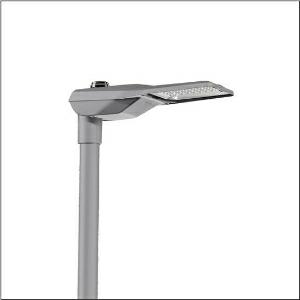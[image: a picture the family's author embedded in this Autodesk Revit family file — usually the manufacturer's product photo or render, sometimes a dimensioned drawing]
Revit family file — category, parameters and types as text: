
# Revit family: streetlight_sl_21_mini___p1_0a_5xe6a37n08hb_d726
name_source: partatom
category: Lighting Fixtures
units: mm (PartAtom-declared; Revit-internal decimal feet)

## family parameters
Cut with Voids When Loaded = No
Host = Face
Light Source = No
Part Type = Normal
Room Calculation Point = No
Round Connector Dimension = Use Diameter
Shared = No

## types (1)
- --- (1 x LED, 9040 lm, 66 W, 3000K)
    Apparent Load = 66 VA
    CIE Flux Codes = 21 50 90 100 100
    Color Rendering = 70
    Color Temperature = 3000K
    Default Elevation = 1800 mm
    Description = Streetlight SL 21 mini, mast luminaire, primary light control with lens, of PMMA, primary optical cover: cover, of toughened safety glass, transparent, light distribution: P1.0a, light emission: direct distribution, primary light characteristic: asymmetric, installation type: side-entry, LED, 3G 1.5mm², High Power LED, rated luminous flux: 9.040lm, luminous efficacy: 137lm/W, light colour: 730, colour temperature: 3000K, control gear: NEMA (7pin), control: overheat protection, pre-setting: linear dimming characteristic, constant luminous flux control, time-dependent luminous flux control, flexible luminous flux parameterisation, mains connection: 230..240V, AC, 50/60Hz, connection cable pre-assembled, cable length: 8,5m, wiring characteristics: H07RN-F, start of lifetime: 66W, end of service life: 69W, reduction: 30W, luminaire housing, of diecast aluminium (EN AC-44300), powder-coated, SITECO metallic grey (DB 702S), corrosivity category C5 high according to DIN EN ISO 12944, multi-level sealing system, sealing non-destructively replaceable, inclination adjustable: 0°, 5°, 10°, 15°, length: 628mm, width: 235mm, height: 110mm, spigot size: 42mm (side-entry), mounting height: 4..8m, protection rating (complete): IP66, insulation class (complete): insulation class I (protective earthing), certification: CE, ENEC, ENEC+, VDE, impact resistance: IK10, permissible operating ambient temperature for outdoor applications: -40..+50°C, standard-compliant lighting for roads and squares, packaging unit: 1 piece

Light Distribution: P1.0a
    Height = 110 mm
    Lamp = 1 x LED
    Lamp Light Flux = 9040 lm
    Lamp Power = 66 W
    Lamp count = 1
    Length = 625 mm
    Luminous efficacy = 137 lm/W
    Manufacturer = Siteco
    ModVariant = No
    Model = 5XE6A37N08HB
    Number of Poles = 1
    OnlyDefault = Yes
    Power Factor = 1
    Product Name = Streetlight SL 21 mini | P1.0a
    Product group = mast luminaire | pylon top
    ProductGroupID = 6100
    Protection Class = Protection class I
    Protection Degree = IP 66
    RLX_Detail_Level = 1
    RLX_Emergency_Light_Flux = 0 lm
    RLX_Emergency_Type = 0
    RLX_Emergency_Type_DB = No
    RlxData = <blob elided: 37437 chars, md5=7955d0b2>
    Socket = socket
    Standby Power = 0 W
    System Light Flux = 9040 lm
    System Power = 66 W
    Type Comments = factory setting: luminous flux: 100 % | dim-lin: 254 | 670 mA
    Type Image = l_1294379.jpg
    URL = http://relux.com
    VarID = @adj_134173
    Voltage = 0 V
    Weight = 0.00 kg
    Width = 234 mm

## geometry (parser evidence)
native form markers: Blend x4, Sweep x11
no freeform markers — native parametric forms only
